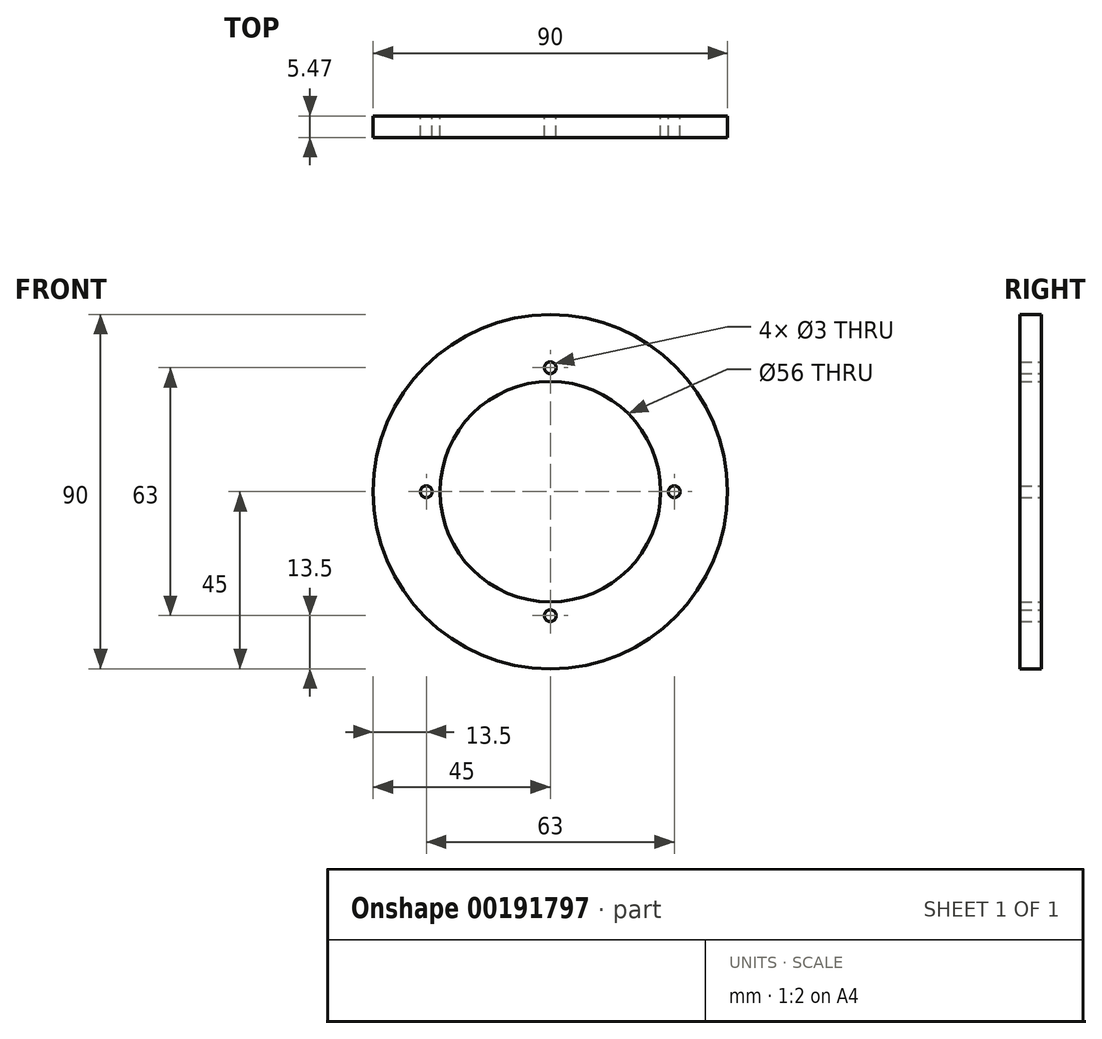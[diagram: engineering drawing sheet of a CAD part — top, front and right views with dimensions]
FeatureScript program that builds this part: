
annotation { "Feature Type Name" : "Feature", "Feature Type Description" : "" }
export const myFeature = defineFeature(function(context is Context, id is Id, definition is map)
    precondition{}
    {
        {
            var Q0;
            Q0=qCreatedBy(makeId("Front.planeOp"),FACE);
            var sketch = newSketch(context, id + "F0", { "sketchPlane" : qUnion([Q0])});
            skCircle(sketch, "E0", {"center": v(0, 0) * mm, "radius": 28 * mm});
            skCircle(sketch, "E1", {"center": v(0, 0) * mm, "radius": 45 * mm});
            skCircle(sketch, "E2", {"center": v(0, 0) * mm, "radius": 31.5 * mm, "construction": true});
            skCircle(sketch, "E3", {"center": v(0, 31.5) * mm, "radius": 1.5 * mm});
            skCircle(sketch, "E4.1.0", {"center": v(-31.5, 0) * mm, "radius": 1.5 * mm});
            skCircle(sketch, "E4.2.0", {"center": v(0, -31.5) * mm, "radius": 1.5 * mm});
            skCircle(sketch, "E4.3.0", {"center": v(31.5, 0) * mm, "radius": 1.5 * mm});
            skSolve(sketch);
        }
        {
            var Q0;
            Q0=makeQuery(id+"F0.imprint","IMPRINT",FACE,{"disambiguationData":[TD([[makeQuery(id+"F0.imprint","IMPRINT",EDGE,{"derivedFrom":sQuery(id+"F0.wireOp",EDGE,"E0")}),-1.0]])]});
            extrude(context, id + "F1", {"entities" : qUnion([Q0]), "depth" : 5.47 * mm});
        }
    });
